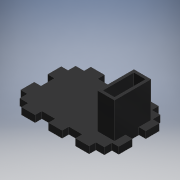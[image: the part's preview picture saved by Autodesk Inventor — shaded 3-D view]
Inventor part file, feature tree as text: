
AUTODESK INVENTOR PART (.ipt)
format: ipt  version: 2019 (Build 230136000, 136)  size: 212,992 bytes
history: native  units: mm
features: extrude x3, sketch x3
ambient origin geometry x8: Origin, YZ Plane, XZ Plane, XY Plane, X Axis, Y Axis, Z Axis, Center Point
bodies: Solid1 (feature_tree)
feature tree (6):
  extrude  "Extrusion1"  Depth=41.0mm
  extrude  "Extrusion2"  Depth=11.0mm
  extrude  "Extrusion3"  Depth=5.5mm
  sketch  "Sketch1"  dims[d0=58.0mm d1=41.0mm]
  sketch  "Sketch2"  dims[d2=11.5mm d3=11.0mm]
  sketch  "Sketch3"  dims[d4=7.0mm d5=5.5mm d6=4.0mm d7=0.0mm d8=1.5mm d9=21.0mm d10=0.0mm d11=4.0mm d12=4.0mm d13=8.0mm d14=8.0mm d15=4.0mm d16=8.0mm d17=21.0mm d18=0.0mm]
